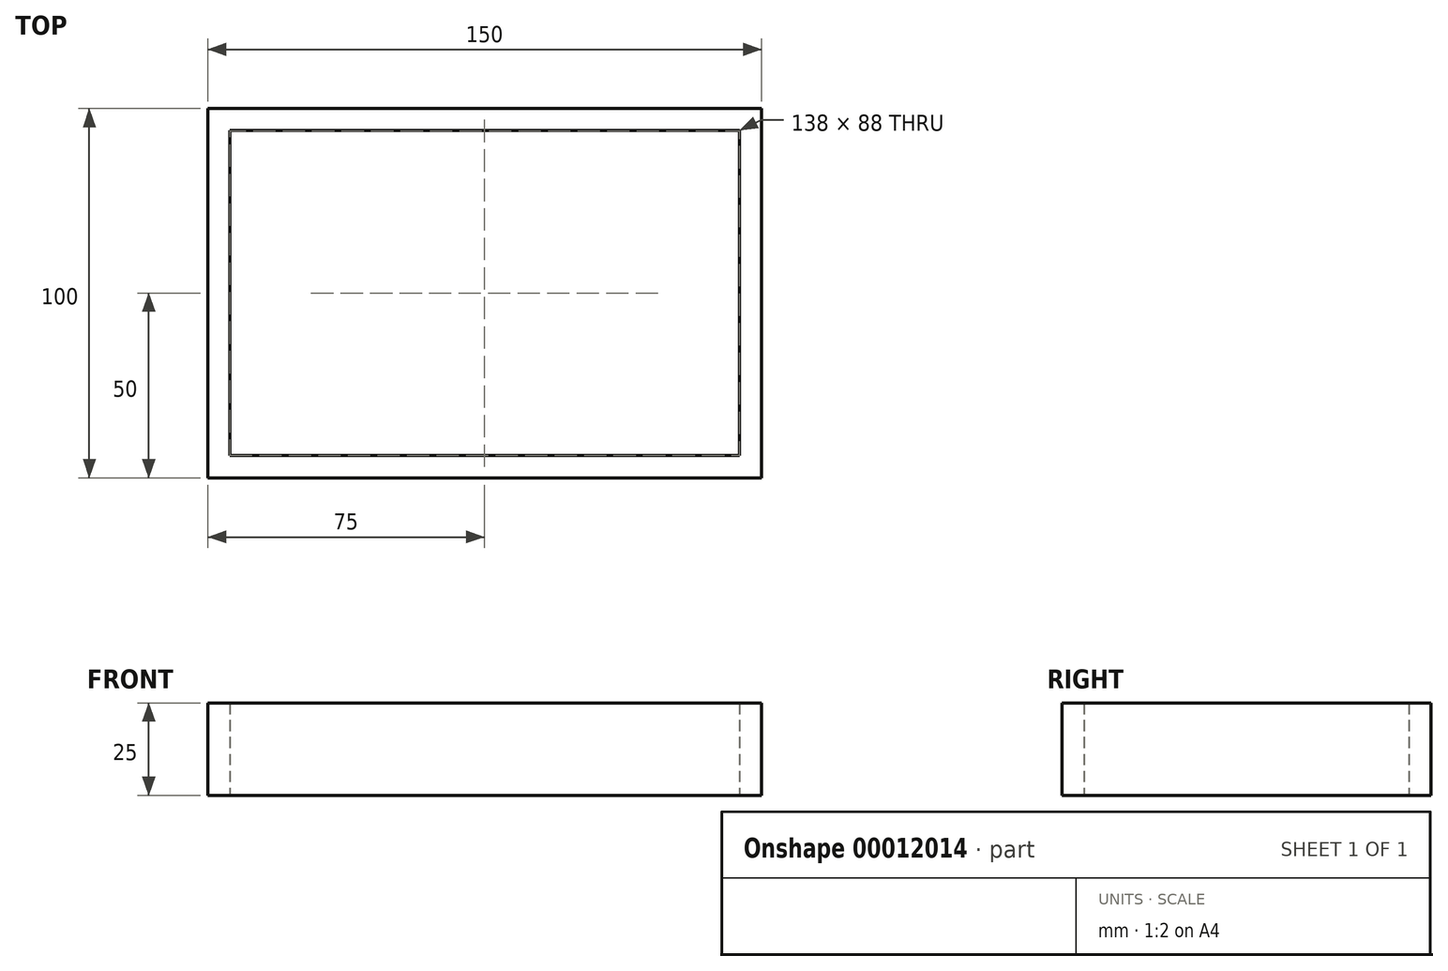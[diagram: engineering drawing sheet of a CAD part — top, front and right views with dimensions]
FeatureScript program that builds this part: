
annotation { "Feature Type Name" : "Feature", "Feature Type Description" : "" }
export const myFeature = defineFeature(function(context is Context, id is Id, definition is map)
    precondition{}
    {
        {
            var Q0;
            Q0=qCreatedBy(makeId("Top.planeOp"),FACE);
            var sketch = newSketch(context, id + "F0", { "sketchPlane" : qUnion([Q0])});
            skLineSegment(sketch, "E0.rect.bottom", {"start": v(75, 50) * mm, "end": v(-75, 50) * mm});
            skLineSegment(sketch, "E0.rect.top", {"start": v(75, -50) * mm, "end": v(-75, -50) * mm});
            skLineSegment(sketch, "E0.rect.left", {"start": v(75, 50) * mm, "end": v(75, -50) * mm});
            skLineSegment(sketch, "E0.rect.right", {"start": v(-75, 50) * mm, "end": v(-75, -50) * mm});
            skPoint(sketch, "E0.rect.middle", {"position": v(0, 0) * mm});
            skPoint(sketch, "E1.visualSharp", {"position": v(-75, 50) * mm});
            skLineSegment(sketch, "E1.filletArc", {"start": v(-75, 50) * mm, "end": v(-75, 50) * mm});
            skPoint(sketch, "E2.visualSharp", {"position": v(-75, -50) * mm});
            skLineSegment(sketch, "E2.filletArc", {"start": v(-75, -50) * mm, "end": v(-75, -50) * mm});
            skPoint(sketch, "E3.visualSharp", {"position": v(75, -50) * mm});
            skLineSegment(sketch, "E3.filletArc", {"start": v(75, -50) * mm, "end": v(75, -50) * mm});
            skPoint(sketch, "E4.visualSharp", {"position": v(75, 50) * mm});
            skLineSegment(sketch, "E4.filletArc", {"start": v(75, 50) * mm, "end": v(75, 50) * mm});
            skLineSegment(sketch, "E5.0", {"start": v(69, 44) * mm, "end": v(-69, 44) * mm});
            skLineSegment(sketch, "E5.1", {"start": v(69, 44) * mm, "end": v(69, -44) * mm});
            skLineSegment(sketch, "E5.2", {"start": v(69, -44) * mm, "end": v(-69, -44) * mm});
            skLineSegment(sketch, "E5.3", {"start": v(-69, 44) * mm, "end": v(-69, -44) * mm});
            skSolve(sketch);
        }
        {
            var Q0;
            Q0=makeQuery(id+"F0.imprint","IMPRINT",FACE,{"disambiguationData":[TD([[makeQuery(id+"F0.imprint","IMPRINT",EDGE,{"derivedFrom":sQuery(id+"F0.wireOp",EDGE,"E0.rect.bottom")}),1.0]])]});
            extrude(context, id + "F1", {"entities" : qUnion([Q0]), "depth" : 25 * mm});
        }
        {
            var Q0;
            Q0=makeQuery(id+"F1.opExtrude","CAP_FACE",FACE,{"disambiguationData":[OSD([sQuery(id+"F0.wireOp",EDGE,"E0.rect.bottom"),sQuery(id+"F0.wireOp",EDGE,"E0.rect.top"),sQuery(id+"F0.wireOp",EDGE,"E0.rect.left"),sQuery(id+"F0.wireOp",EDGE,"E0.rect.right"),sQuery(id+"F0.wireOp",EDGE,"E5.0"),sQuery(id+"F0.wireOp",EDGE,"E5.1"),sQuery(id+"F0.wireOp",EDGE,"E5.2"),sQuery(id+"F0.wireOp",EDGE,"E5.3")])],"isStart":false});
            var sketch = newSketch(context, id + "F2", { "sketchPlane" : qUnion([Q0])});
            skLineSegment(sketch, "E6", {"start": v(-69, 44) * mm, "end": v(-75, 50) * mm});
            skLineSegment(sketch, "E7", {"start": v(-75, -50) * mm, "end": v(-69, -44) * mm});
            skLineSegment(sketch, "E8", {"start": v(75, -50) * mm, "end": v(69, -44) * mm});
            skLineSegment(sketch, "E9", {"start": v(69, 44) * mm, "end": v(75, 50) * mm});
            skSolve(sketch);
        }
        {
            var Q0;
            Q0 = qSketchRegion(id + "F2", true);
            var Q1;
            Q1 = qConstructionFilter(qBodyType(qCreatedBy(id + "F2" ,EDGE), BodyType.WIRE), ConstructionObject.NO);
            extrude(context, id + "F3", {"entities" : qUnion([Q0]), "bodyType" : ToolBodyType.SURFACE, "operationType" : NewBodyOperationType.REMOVE, "surfaceEntities" : qUnion([Q1]), "endBound" : BoundingType.UP_TO_NEXT, "oppositeDirection" : true, "depth" : 25 * mm});
        }
    });
